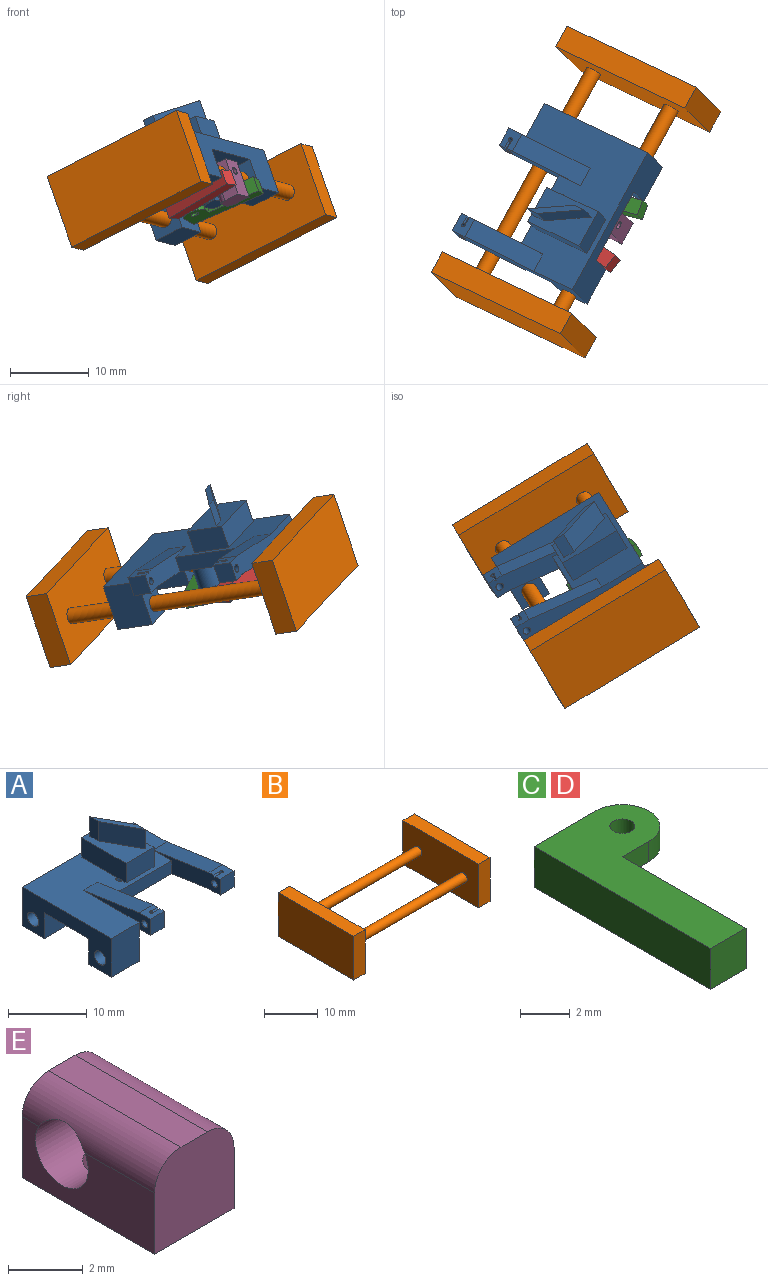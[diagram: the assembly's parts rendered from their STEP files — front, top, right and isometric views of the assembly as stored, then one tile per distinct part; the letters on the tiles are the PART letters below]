
ASSEMBLY  parts=5 mates=4
PART A: 61 faces, bbox 20x18x13 mm
  f0: plane 20x16mm, normal (0,0,1), area 162.9mm2, adj f2,f3,f8,f10,f13,f14,f15,f27
  f1: plane 8x5mm, normal (0,0,1), area 35.5mm2, adj f41,f42,f43,f44,f45,f46,f47,f48
  f2: plane 12x3.5mm, normal (-1,0,0), area 21.7mm2, adj f0,f11,f30,f31,f32,f33,f35,f36
  f3: plane 12x3.5mm, normal (1,0,0), area 21.7mm2, adj f0,f4,f7,f27,f28,f29,f34,f38
  f4: plane 2.5x2mm, normal (0,0,1), area 4.4mm2, adj f3,f5,f7,f10,f27,f38,f39
  f5: cylinder r=0.25mm len=0.82mm, axis (0,0,1), area 1.2mm2, adj f4,f34,f38,f39
  f6: cylinder r=0.25mm len=0.82mm, axis (0,0,1), area 1.2mm2, adj f30,f35,f36,f37
  f7: plane 2.5x2.5mm, normal (0,-1,0), area 6.2mm2, adj f3,f4,f10,f29
  f8: plane 18x7.5mm, normal (1,0,0), area 53.2mm2, adj f0,f9,f11,f13,f21,f23,f24,f30
  f9: plane 20x12mm, normal (0,0,-1), area 147.4mm2, adj f8,f12,f13,f14,f16,f18,f19,f21
  f10: plane 12x2.5mm, normal (-1,0,0), area 11.7mm2, adj f0,f4,f7,f15,f27,f29,f34
  f11: plane 2.5x2.5mm, normal (0,-1,0), area 6.3mm2, adj f2,f8,f30,f32
  f12: plane 6.67x5mm, normal (1,0,0), area 16.2mm2, adj f9,f15,f16,f17,f26,f28
  f13: plane 20x6mm, normal (0,1,0), area 80mm2, adj f0,f8,f9,f14,f18,f20,f22,f23
  f14: plane 16x6mm, normal (-1,0,0), area 57.7mm2, adj f0,f9,f13,f15,f16,f17,f19,f20
  f15: plane 6x5mm, normal (0,-1,0), area 30mm2, adj f0,f10,f12,f14,f17
  f16: plane 5x4mm, normal (0,1,0), area 20mm2, adj f9,f12,f14,f17
  f17: plane 5x4mm, normal (0,0,-1), area 20mm2, adj f12,f14,f15,f16
  f18: plane 4x4mm, normal (1,0,0), area 12.9mm2, adj f9,f13,f19,f20,f25
  f19: plane 5x4mm, normal (0,-1,0), area 20mm2, adj f9,f14,f18,f20
  f20: plane 5x4mm, normal (0,0,-1), area 20mm2, adj f13,f14,f18,f19
  f21: plane 5x4mm, normal (0,-1,0), area 20mm2, adj f8,f9,f22,f23
  f22: plane 4x4mm, normal (-1,0,0), area 12.9mm2, adj f9,f13,f21,f23,f24
  f23: plane 5x4mm, normal (0,0,-1), area 20mm2, adj f8,f13,f21,f22
  f24: cylinder r=1mm len=5mm, axis (1,0,0), area 31.4mm2, adj f8,f22
  f25: cylinder r=1mm len=5mm, axis (1,0,0), area 31.4mm2, adj f14,f18
  f26: cylinder r=1mm len=5mm, axis (1,0,0), area 31.4mm2, adj f12,f14
  f27: plane 10x2.5mm, normal (0,0.15,0.99), area 25.3mm2, adj f0,f3,f4,f10
  f28: plane 6.67x2.5mm, normal (0,-0.15,-0.99), area 16.9mm2, adj f3,f9,f12,f29
  f29: plane 2.5x2mm, normal (0,0,-1), area 5mm2, adj f3,f7,f10,f28
  f30: plane 2.5x2mm, normal (0,0,1), area 4.4mm2, adj f2,f6,f8,f11,f31,f36,f37
  f31: plane 10x2.5mm, normal (0,0.15,0.99), area 25.3mm2, adj f0,f2,f8,f30
  f32: plane 2.5x2mm, normal (0,0,-1), area 5mm2, adj f2,f8,f11,f33
  f33: plane 6.67x2.5mm, normal (0,-0.15,-0.99), area 16.9mm2, adj f2,f8,f9,f32
  f34: cylinder r=0.5mm len=2.5mm, axis (1,0,0), area 7.7mm2, adj f3,f5,f10
  f35: cylinder r=0.5mm len=2.5mm, axis (1,0,0), area 7.7mm2, adj f2,f6,f8
  f36: plane 1.1x0.2mm, normal (0,-0.71,0.71), area 0.3mm2, adj f2,f6,f30,f37
  f37: plane 1.1x0.2mm, normal (0,0.71,0.71), area 0.3mm2, adj f2,f6,f30,f36
  f38: plane 1.1x0.2mm, normal (0,0.71,0.71), area 0.3mm2, adj f3,f4,f5,f39
  f39: plane 1.1x0.2mm, normal (0,-0.71,0.71), area 0.3mm2, adj f3,f4,f5,f38
  f40: plane 10x2mm, normal (0,-1,0), area 20mm2, adj f0,f2,f3,f9
  f41: plane 8x3mm, normal (1,0,0), area 24mm2, adj f0,f1,f42,f44
  f42: plane 5x3mm, normal (0,1,0), area 15mm2, adj f0,f1,f41,f43
  f43: plane 8x3mm, normal (-1,0,0), area 24mm2, adj f0,f1,f42,f44,f58
  f44: plane 5x3mm, normal (0,-1,0), area 15mm2, adj f0,f1,f41,f43
  f45: plane 3x1.5mm, normal (-1,0,0), area 4.5mm2, adj f1,f46,f48,f49
  f46: plane 5.5x3mm, normal (-0.88,-0.48,0), area 18.8mm2, adj f1,f45,f47,f49
  f47: plane 3x1.5mm, normal (1,0,0), area 4.5mm2, adj f1,f46,f48,f49
  f48: plane 5.5x3mm, normal (0.88,0.48,0), area 18.8mm2, adj f1,f45,f47,f49
  f49: plane 7x3mm, normal (0,0,1), area 4.5mm2, adj f45,f46,f47,f48
  f50: cylinder r=1.5mm len=3mm, axis (0,0,1), area 28.3mm2, adj f9,f51
  f51: plane 3x3mm, normal (0,0,-1), area 6.3mm2, adj f50,f57
  f52: plane 5x3mm, normal (0,1,0), area 15mm2, adj f9,f53,f55,f56
  f53: plane 5x1mm, normal (1,0,0), area 5mm2, adj f9,f52,f56,f59
  f54: plane 5x1mm, normal (0,-1,0), area 5mm2, adj f9,f56,f59,f60
  f55: plane 5x1mm, normal (-1,0,0), area 5mm2, adj f9,f52,f56,f60
  f56: plane 3x2mm, normal (0,0,-1), area 5.6mm2, adj f52,f53,f54,f55,f59,f60
  f57: cylinder r=0.5mm len=5mm, axis (0,0,-1), area 15.7mm2, adj f0,f51,f58
  f58: plane 1x0.5mm, normal (0,0,-1), area 0.4mm2, adj f43,f57
  f59: cylinder r=1mm len=5mm, axis (0,0,1), area 7.9mm2, adj f9,f53,f54,f56
  f60: cylinder r=1mm len=5mm, axis (0,0,-1), area 7.9mm2, adj f9,f54,f55,f56
PART B: 14 faces, bbox 36x20x10 mm
  f0: plane 10x3mm, normal (0,-1,0), area 30mm2, adj f1,f3,f4,f5
  f1: plane 20x10mm, normal (1,0,0), area 193.7mm2, adj f0,f2,f4,f5,f12,f13
  f2: plane 10x3mm, normal (0,1,0), area 30mm2, adj f1,f3,f4,f5
  f3: plane 20x10mm, normal (-1,0,0), area 200mm2, adj f0,f2,f4,f5
  f4: plane 20x3mm, normal (0,0,1), area 60mm2, adj f0,f1,f2,f3
  f5: plane 20x3mm, normal (0,0,-1), area 60mm2, adj f0,f1,f2,f3
  f6: plane 20x10mm, normal (-1,0,0), area 193.7mm2, adj f7,f9,f10,f11,f12,f13
  f7: plane 10x3mm, normal (0,-1,0), area 30mm2, adj f6,f8,f10,f11
  f8: plane 20x10mm, normal (1,0,0), area 200mm2, adj f7,f9,f10,f11
  f9: plane 10x3mm, normal (0,1,0), area 30mm2, adj f6,f8,f10,f11
  f10: plane 20x3mm, normal (0,0,1), area 60mm2, adj f6,f7,f8,f9
  f11: plane 20x3mm, normal (0,0,-1), area 60mm2, adj f6,f7,f8,f9
  f12: cylinder r=1mm len=30mm, axis (-1,0,0), area 188.5mm2, adj f1,f6
  f13: cylinder r=1mm len=30mm, axis (-1,0,0), area 188.5mm2, adj f1,f6
PART C: 10 faces, bbox 5x10x2 mm
  f0: plane 3.5x2mm, normal (0,1,0), area 5.5mm2, adj f2,f3,f5,f7,f8,f9
  f1: cylinder r=0.5mm len=1mm, axis (0,0,-1), area 3.1mm2, adj f8,f9
  f2: plane 10x2mm, normal (0,0,-1), area 20mm2, adj f0,f3,f4,f5
  f3: plane 10x2mm, normal (-1,0,0), area 20mm2, adj f0,f2,f4,f8
  f4: plane 2x2mm, normal (0,-1,0), area 4mm2, adj f2,f3,f5,f8
  f5: plane 10x2mm, normal (1,0,0), area 17mm2, adj f0,f2,f4,f6,f8,f9
  f6: plane 1.5x1mm, normal (0,-1,0), area 1.5mm2, adj f5,f7,f8,f9
  f7: cylinder r=1.5mm len=3mm, axis (0,0,-1), area 4.7mm2, adj f0,f6,f8,f9
  f8: plane 10x5mm, normal (0,0,1), area 27.2mm2, adj f0,f1,f3,f4,f5,f6,f7
  f9: plane 3x3mm, normal (0,0,-1), area 7.2mm2, adj f0,f1,f5,f6,f7
PART D: same geometry as C
PART E: 10 faces, bbox 3x5x3 mm
  f0: plane 5x2mm, normal (1,0,0), area 7.5mm2, adj f1,f4,f5,f7,f9
  f1: plane 3x3mm, normal (0,1,0), area 8.6mm2, adj f0,f2,f3,f4,f8,f9
  f2: plane 5x2mm, normal (-1,0,0), area 7.5mm2, adj f1,f4,f5,f7,f8
  f3: plane 5x1mm, normal (0,0,1), area 5mm2, adj f1,f7,f8,f9
  f4: plane 5x3mm, normal (0,0,-1), area 14.2mm2, adj f0,f1,f2,f6,f7
  f5: cylinder r=1mm len=3mm, axis (-1,0,0), area 17.8mm2, adj f0,f2,f6,f8,f9
  f6: cylinder r=0.5mm len=1mm, axis (0,0,-1), area 1.8mm2, adj f4,f5
  f7: plane 3x3mm, normal (0,-1,0), area 8.6mm2, adj f0,f2,f3,f4,f8,f9
  f8: cylinder r=1mm len=5mm, axis (0,1,0), area 7.2mm2, adj f1,f2,f3,f5,f7
  f9: cylinder r=1mm len=5mm, axis (0,-1,0), area 7.2mm2, adj f0,f1,f3,f5,f7
PLACE A rot(axis=(0.06,-0.25,-0.97),119deg) t=(33.97,-9.5,2.12)mm
PLACE B rot(axis=(0.06,-0.25,-0.97),119deg) t=(35.59,-8.31,0.05)mm
PLACE C rot(axis=(-0.58,0.79,-0.22),175.8deg) t=(34.48,-8.88,-1.25)mm
PLACE D rot(axis=(-0.43,-0.15,0.89),58.4deg) t=(33.94,-11.6,-2.74)mm
PLACE E rot(axis=(0.42,-0.78,-0.46),142.7deg) t=(39.8,-11.96,2.76)mm
MATE revolute D.f1 <-> A.f50  axis (-0.31,0.31,0.9) through (35.32,-10.61,-0.37)mm
MATE slider A.f24 <-> B.f13  axis (0.48,0.87,-0.13) through (44.31,-3.77,1.55)mm
MATE slider E.f5 <-> B.f13  axis (-0.48,-0.87,0.13) through (39.08,-13.26,2.95)mm
MATE revolute C.f1 <-> A.f50  axis (-0.31,0.31,0.9) through (35.64,-10.92,-1.27)mm
